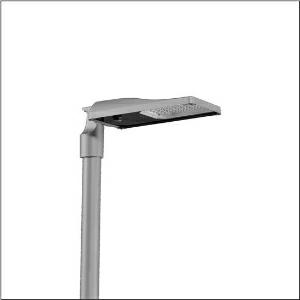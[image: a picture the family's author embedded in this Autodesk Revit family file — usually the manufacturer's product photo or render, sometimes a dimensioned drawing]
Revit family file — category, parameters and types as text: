
# Revit family: streetlight_sl_31_mini___st1_0a_5xh6d3ar08ha_e09e
name_source: partatom
category: Lighting Fixtures
units: mm (PartAtom-declared; Revit-internal decimal feet)

## family parameters
Cut with Voids When Loaded = No
Host = Face
Light Source = No
Part Type = Normal
Room Calculation Point = No
Round Connector Dimension = Use Diameter
Shared = No

## types (1)
- --- (1 x LED, 9230 lm, 68.3 W, 3000K)
    Apparent Load = 68 VA
    CIE Flux Codes = 37 72 97 100 100
    Color Rendering = 70
    Color Temperature = 3000K
    Default Elevation = 1800 mm
    Description = Streetlight SL 31 mini D4i mast luminaire for post-top, side-entry; light control with lens of PMMA; light distribution: ST1.0a, direct asymmetric distribution, for standard-compliant lighting for roads and squares; LED: luminous flux: 9.230lm, light colour: 730, colour temperature: 3000K; luminous efficacy: 135,1lm/W; control: pre-setting: logarithmic dimming characteristic, flexible luminous flux parameterisation, time-dependent luminous flux control, constant luminous flux control, power reduction, intelligent temperature release in ECG and LED module, overheat protection; luminaire housing, of diecast aluminium, SITECO metallic grey (DB 702S), corrosivity category C5 high according to DIN EN ISO 12944; cover of toughened safety glass, transparent, opened without tools; mast flange of diecast aluminium, SITECO metallic grey (DB 702S), spigot size: 76/60mm, mast flange included unmounted; cable length: 8,5m, connection cable pre-assembled; mains connection: 220..240V, AC, 50/60Hz; power consumption (at start of service life): 68,3W / (at end of service life): 74,5W / (with reduced operation 50%): 29,5W; protection rating (complete): IP66; insulation class (complete): insulation class II (safety insulation); impact resistance: IK09; certification: CE, ENEC, ENEC+, VDE, UKCA, ZD4i; permissible operating ambient temperature for outdoor applications: -40..+50°C; packaging unit: 1 piece

Light Distribution: ST1.0a
    Height = 76 mm
    Lamp = 1 x LED
    Lamp Light Flux = 9230 lm
    Lamp Power = 68.3 W
    Lamp count = 1
    Length = 547 mm
    Luminous efficacy = 135 lm/W
    Manufacturer = Siteco
    ModVariant = No
    Model = 5XH6D3AR08HA
    Number of Poles = 1
    OnlyDefault = Yes
    Power Factor = 1
    Product Name = Streetlight SL 31 mini | ST1.0a
    Product group = mast luminaire | pylon top
    ProductGroupID = 6100
    Protection Class = Protection class II
    Protection Degree = IP 66
    RLX_Detail_Level = 1
    RLX_Emergency_Light_Flux = 0 lm
    RLX_Emergency_Type = 0
    RLX_Emergency_Type_DB = No
    RlxData = <blob elided: 24157 chars, md5=14368f01>
    Socket = socket
    Standby Power = 0 W
    System Light Flux = 9230 lm
    System Power = 68 W
    Type Comments = factory setting: luminous flux: 100 % | dim-lin: 254 | 692 mA
    Type Image = l_1300328.jpg
    URL = http://relux.com
    VarID = @adj_020397
    Voltage = 0 V
    Weight = 0.00 kg
    Width = 265 mm

## geometry (parser evidence)
native form markers: Blend x4, Sweep x11
no freeform markers — native parametric forms only
